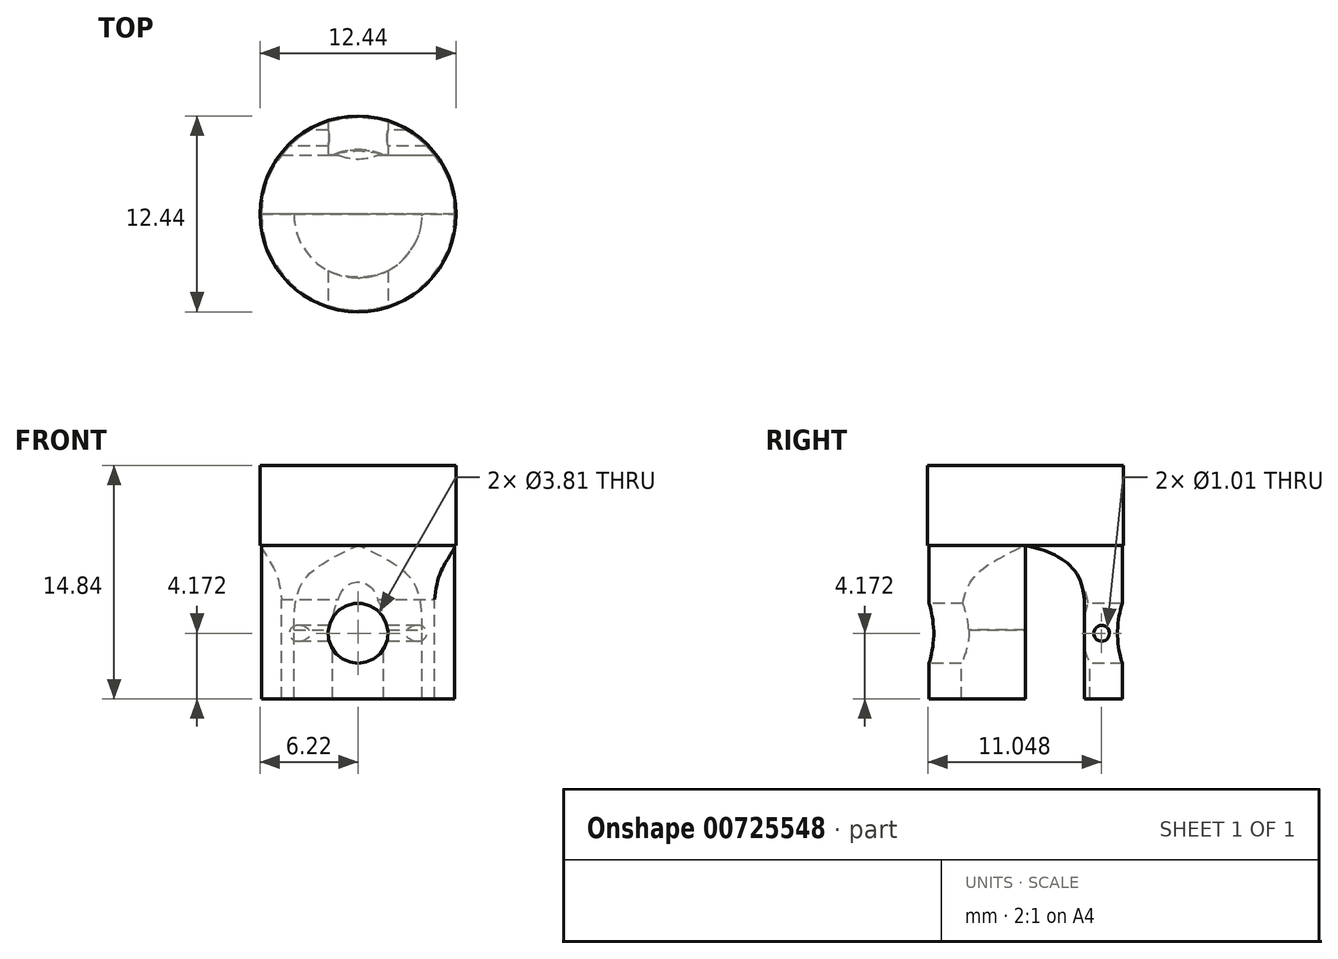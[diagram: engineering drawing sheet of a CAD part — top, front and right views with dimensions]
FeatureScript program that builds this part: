
annotation { "Feature Type Name" : "Feature", "Feature Type Description" : "" }
export const myFeature = defineFeature(function(context is Context, id is Id, definition is map)
    precondition{}
    {
        {
            var Q0;
            Q0=qCreatedBy(makeId("Top.planeOp"),FACE);
            var sketch = newSketch(context, id + "F0", { "sketchPlane" : qUnion([Q0])});
            skCircle(sketch, "E0", {"center": v(0, 0) * mm, "radius": 6.22 * mm});
            skSolve(sketch);
        }
        {
            var Q0;
            Q0=makeQuery(id+"F0.imprint","IMPRINT",FACE,{"disambiguationData":[TD([[makeQuery(id+"F0.imprint","IMPRINT",EDGE,{"derivedFrom":sQuery(id+"F0.wireOp",EDGE,"E0")}),1.0]])]});
            extrude(context, id + "F1", {"entities" : qUnion([Q0]), "depth" : 5.08 * mm, "offsetDistance" : 25.4 * mm});
        }
        {
            var Q0;
            Q0=qCreatedBy(makeId("Front.planeOp"),FACE);
            var sketch = newSketch(context, id + "F2", { "sketchPlane" : qUnion([Q0])});
            skLineSegment(sketch, "E1", {"start": v(0, 0) * mm, "end": v(-6.14, 0) * mm});
            skLineSegment(sketch, "E2", {"start": v(-6.14, 0) * mm, "end": v(-6.14, -9.76) * mm});
            skLineSegment(sketch, "E3", {"start": v(-6.14, -9.76) * mm, "end": v(-4.08, -9.76) * mm});
            skLineSegment(sketch, "E4", {"start": v(-4.08, -9.76) * mm, "end": v(-4.08, -5.38) * mm});
            skFitSpline(sketch, "E5", {"points": [v(-4.08, -5.38) * mm, v(-3.48, -2.3) * mm, v(0, 0) * mm], "startDerivative": vector(0.08, 7.2) * mm, "endDerivative": vector(7.9, 3.66) * mm});
            skLineSegment(sketch, "E6", {"start": v(-6.14, 0) * mm, "end": v(0, 0) * mm});
            skSolve(sketch);
        }
        {
            var Q0;
            Q0=qCreatedBy(makeId("Front.planeOp"),FACE);
            var sketch = newSketch(context, id + "F3", { "sketchPlane" : qUnion([Q0])});
            skLineSegment(sketch, "E7", {"start": v(0, 27.07) * mm, "end": v(0, -23.05) * mm});
            skSolve(sketch);
        }
        {
            var Q0;
            Q0=makeQuery(id+"F2.imprint","IMPRINT",FACE,{"disambiguationData":[TD([[makeQuery(id+"F2.imprint","IMPRINT",EDGE,{"derivedFrom":sQuery(id+"F2.wireOp",EDGE,"E2")}),1.0]])]});
            var Q1;
            Q1=sQuery(id+"F3.wireOp",EDGE,"E7");
            revolve(context, id + "F4", {"surfaceOperationType" : NewSurfaceOperationType.NEW, "entities" : qUnion([Q0]), "axis" : qUnion([Q1]), "revolveType" : RevolveType.ONE_DIRECTION, "angle" : 359.9 * degree});
        }
        {
            var Q0;
            Q0=qCreatedBy(makeId("Right.planeOp"),FACE);
            var sketch = newSketch(context, id + "F5", { "sketchPlane" : qUnion([Q0])});
            skLineSegment(sketch, "E8", {"start": v(3.74, -10.06) * mm, "end": v(3.74, -3.45) * mm});
            skFitSpline(sketch, "E9", {"points": [v(3.74, -3.45) * mm, v(3.25, -1.8) * mm, v(1.8, -0.6) * mm, v(0, 0) * mm], "startDerivative": vector(-0.85, 5.36) * mm, "endDerivative": vector(-5.38, 1.37) * mm});
            skLineSegment(sketch, "E10", {"start": v(0, 0) * mm, "end": v(0, -9.96) * mm});
            skLineSegment(sketch, "E11", {"start": v(0, -9.96) * mm, "end": v(3.74, -10.06) * mm});
            skSolve(sketch);
        }
        {
            var Q0;
            Q0=makeQuery(id+"FpqluffpEJwd9sQ_2.1.F5.imprint","IMPRINT",FACE,{"disambiguationData":[TD([[makeQuery(id+"FpqluffpEJwd9sQ_2.1.F5.imprint","IMPRINT",EDGE,{"derivedFrom":sQuery(id+"FpqluffpEJwd9sQ_2.1.F5.wireOp",EDGE,"E8")}),1.0]])]});
            var Q1;
            Q1=makeQuery(id+"F5.imprint","IMPRINT",FACE,{"disambiguationData":[TD([[makeQuery(id+"F5.imprint","IMPRINT",EDGE,{"derivedFrom":sQuery(id+"F5.wireOp",EDGE,"E8")}),1.0]])]});
            extrude(context, id + "F6", {"entities" : qUnion([Q0, Q1]), "operationType" : NewBodyOperationType.REMOVE, "endBound" : BoundingType.SYMMETRIC, "oppositeDirection" : true, "depth" : 25.4 * mm, "offsetDistance" : 25.4 * mm});
        }
        {
            var Q0;
            Q0=qCreatedBy(makeId("Front.planeOp"),FACE);
            var sketch = newSketch(context, id + "F7", { "sketchPlane" : qUnion([Q0])});
            skCircle(sketch, "E12", {"center": v(0, -5.59) * mm, "radius": 1.9 * mm});
            skSolve(sketch);
        }
        {
            var Q0;
            Q0=makeQuery(id+"F7.imprint","IMPRINT",FACE,{"disambiguationData":[TD([[makeQuery(id+"F7.imprint","IMPRINT",EDGE,{"derivedFrom":sQuery(id+"F7.wireOp",EDGE,"E12")}),1.0]])]});
            extrude(context, id + "F8", {"entities" : qUnion([Q0]), "operationType" : NewBodyOperationType.REMOVE, "endBound" : BoundingType.SYMMETRIC, "oppositeDirection" : true, "depth" : 25.4 * mm, "offsetDistance" : 25.4 * mm});
        }
        {
            var Q0;
            Q0=qCreatedBy(makeId("Right.planeOp"),FACE);
            var sketch = newSketch(context, id + "F9", { "sketchPlane" : qUnion([Q0])});
            skLineSegment(sketch, "E13", {"start": v(6.02, -3.72) * mm, "end": v(6.02, -7.46) * mm});
            skLineSegment(sketch, "E14", {"start": v(6.02, -5.59) * mm, "end": v(-6.7, -5.59) * mm});
            skCircle(sketch, "E15", {"center": v(4.83, -5.59) * mm, "radius": 0.5 * mm});
            skSolve(sketch);
        }
        {
            var Q0;
            {var subQ0=sQuery(id+"F9.wireOp",EDGE,"E15");var subQ1=sQuery(id+"F9.wireOp",EDGE,"E14");var subQ2=makeQuery(id+"F9.imprint","INTERSECT",VERTEX,{"disambiguationData":[OD(0.0)],"derivedFrom":[subQ1,subQ0]});Q0=makeQuery(id+"F9.imprint","IMPRINT",FACE,{"disambiguationData":[TD([[makeQuery(id+"F9.imprint","IMPRINT",EDGE,{"disambiguationData":[TD([[subQ2,1.0]])],"derivedFrom":subQ1}),-1.0]])]});}
            var Q1;
            {var subQ0=sQuery(id+"F9.wireOp",EDGE,"E15");var subQ1=sQuery(id+"F9.wireOp",EDGE,"E14");var subQ2=makeQuery(id+"F9.imprint","INTERSECT",VERTEX,{"disambiguationData":[OD(0.0)],"derivedFrom":[subQ1,subQ0]});Q1=makeQuery(id+"F9.imprint","IMPRINT",FACE,{"disambiguationData":[TD([[makeQuery(id+"F9.imprint","IMPRINT",EDGE,{"disambiguationData":[TD([[subQ2,1.0]])],"derivedFrom":subQ1}),1.0]])]});}
            extrude(context, id + "F10", {"entities" : qUnion([Q0, Q1]), "operationType" : NewBodyOperationType.REMOVE, "endBound" : BoundingType.SYMMETRIC, "depth" : 25.4 * mm, "offsetDistance" : 25.4 * mm});
        }
    });
